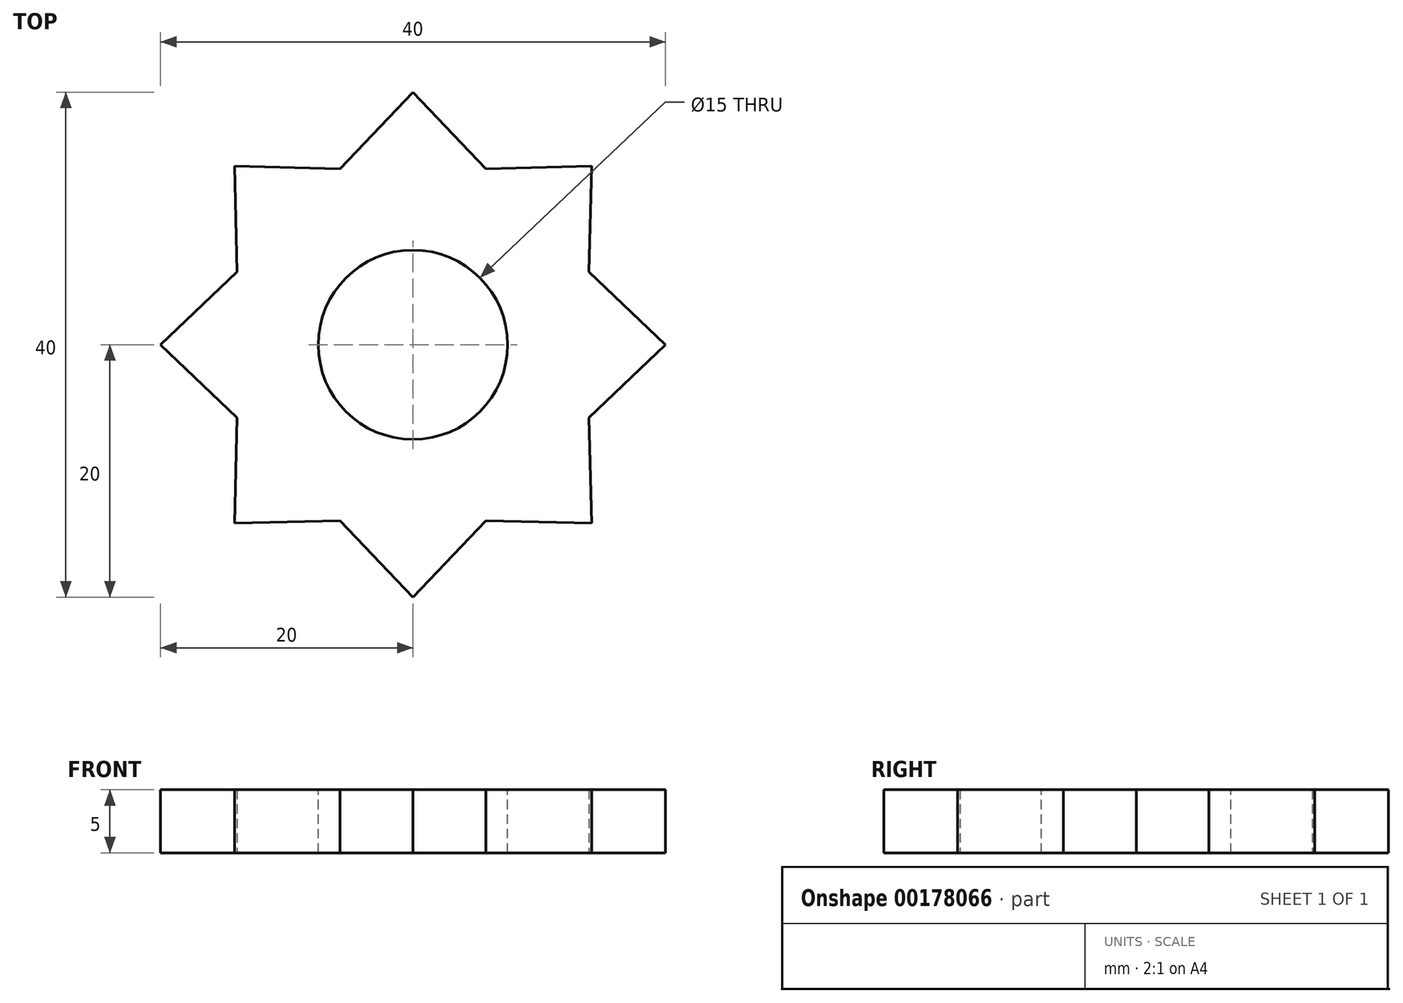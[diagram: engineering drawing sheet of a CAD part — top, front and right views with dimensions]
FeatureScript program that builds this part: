
annotation { "Feature Type Name" : "Feature", "Feature Type Description" : "" }
export const myFeature = defineFeature(function(context is Context, id is Id, definition is map)
    precondition{}
    {
        {
            var Q0;
            Q0=qCreatedBy(makeId("Top.planeOp"),FACE);
            var sketch = newSketch(context, id + "F0", { "sketchPlane" : qUnion([Q0])});
            skCircle(sketch, "E0", {"center": v(0, 0) * mm, "radius": 15 * mm});
            skLineSegment(sketch, "E1", {"start": v(0, 0) * mm, "end": v(0, 15) * mm, "construction": true});
            skLineSegment(sketch, "E2", {"start": v(0, 15) * mm, "end": v(0, 20) * mm});
            skLineSegment(sketch, "E3", {"start": v(0, 20) * mm, "end": v(5.94, 13.78) * mm});
            skLineSegment(sketch, "E4.MirrorCS", {"start": v(0, 20) * mm, "end": v(-5.94, 13.78) * mm});
            skLineSegment(sketch, "E5.1.0", {"start": v(-14.14, 14.14) * mm, "end": v(-13.94, 5.54) * mm});
            skLineSegment(sketch, "E5.1.1", {"start": v(-14.14, 14.14) * mm, "end": v(-5.54, 13.94) * mm});
            skLineSegment(sketch, "E5.2.0", {"start": v(-20, 0) * mm, "end": v(-13.78, -5.94) * mm});
            skLineSegment(sketch, "E5.2.1", {"start": v(-20, 0) * mm, "end": v(-13.78, 5.94) * mm});
            skLineSegment(sketch, "E5.3.0", {"start": v(-14.14, -14.14) * mm, "end": v(-5.54, -13.94) * mm});
            skLineSegment(sketch, "E5.3.1", {"start": v(-14.14, -14.14) * mm, "end": v(-13.94, -5.54) * mm});
            skLineSegment(sketch, "E5.4.0", {"start": v(0, -20) * mm, "end": v(5.94, -13.78) * mm});
            skLineSegment(sketch, "E5.4.1", {"start": v(0, -20) * mm, "end": v(-5.94, -13.78) * mm});
            skLineSegment(sketch, "E5.5.0", {"start": v(14.14, -14.14) * mm, "end": v(13.94, -5.54) * mm});
            skLineSegment(sketch, "E5.5.1", {"start": v(14.14, -14.14) * mm, "end": v(5.54, -13.94) * mm});
            skLineSegment(sketch, "E5.6.0", {"start": v(20, 0) * mm, "end": v(13.78, 5.94) * mm});
            skLineSegment(sketch, "E5.6.1", {"start": v(20, 0) * mm, "end": v(13.78, -5.94) * mm});
            skLineSegment(sketch, "E5.7.0", {"start": v(14.14, 14.14) * mm, "end": v(5.54, 13.94) * mm});
            skLineSegment(sketch, "E5.7.1", {"start": v(14.14, 14.14) * mm, "end": v(13.94, 5.54) * mm});
            skSolve(sketch);
        }
        {
            var Q0;
            Q0 = qSketchRegion(id + "F0", true);
            var Q1;
            {var subQ0=sQuery(id+"F0.wireOp",EDGE,"E0");var subQ3=makeQuery(id+"F0.imprint","INTERSECT",VERTEX,{"derivedFrom":[subQ0,sQuery(id+"F0.wireOp",EDGE,"E5.6.0")]});Q1=makeQuery(id+"F0.imprint","IMPRINT",FACE,{"disambiguationData":[TD([[makeQuery(id+"F0.imprint","IMPRINT",EDGE,{"disambiguationData":[TD([[subQ3,1.0]])],"derivedFrom":subQ0}),1.0]])]});}
            extrude(context, id + "F1", {"entities" : qUnion([Q0, Q1]), "depth" : 5 * mm});
        }
        {
            var Q0;
            Q0=makeQuery(id+"F1.opExtrude","CAP_FACE",FACE,{"disambiguationData":[OSD([sQuery(id+"F0.wireOp",EDGE,"E3"),sQuery(id+"F0.wireOp",EDGE,"E4.MirrorCS"),sQuery(id+"F0.wireOp",EDGE,"E5.1.0"),sQuery(id+"F0.wireOp",EDGE,"E5.1.1"),sQuery(id+"F0.wireOp",EDGE,"E5.2.0"),sQuery(id+"F0.wireOp",EDGE,"E5.2.1"),sQuery(id+"F0.wireOp",EDGE,"E5.3.0"),sQuery(id+"F0.wireOp",EDGE,"E5.3.1"),sQuery(id+"F0.wireOp",EDGE,"E5.4.0"),sQuery(id+"F0.wireOp",EDGE,"E5.4.1"),sQuery(id+"F0.wireOp",EDGE,"E5.5.0"),sQuery(id+"F0.wireOp",EDGE,"E5.5.1"),sQuery(id+"F0.wireOp",EDGE,"E5.6.0"),sQuery(id+"F0.wireOp",EDGE,"E5.6.1"),sQuery(id+"F0.wireOp",EDGE,"E5.7.0"),sQuery(id+"F0.wireOp",EDGE,"E5.7.1")])],"isStart":false});
            var sketch = newSketch(context, id + "F2", { "sketchPlane" : qUnion([Q0])});
            skCircle(sketch, "E6", {"center": v(0, 0) * mm, "radius": 7.5 * mm});
            skSolve(sketch);
        }
        {
            var Q0;
            Q0 = qSketchRegion(id + "F2", true);
            extrude(context, id + "F3", {"entities" : qUnion([Q0]), "operationType" : NewBodyOperationType.REMOVE, "oppositeDirection" : true, "depth" : 25 * mm});
        }
    });
